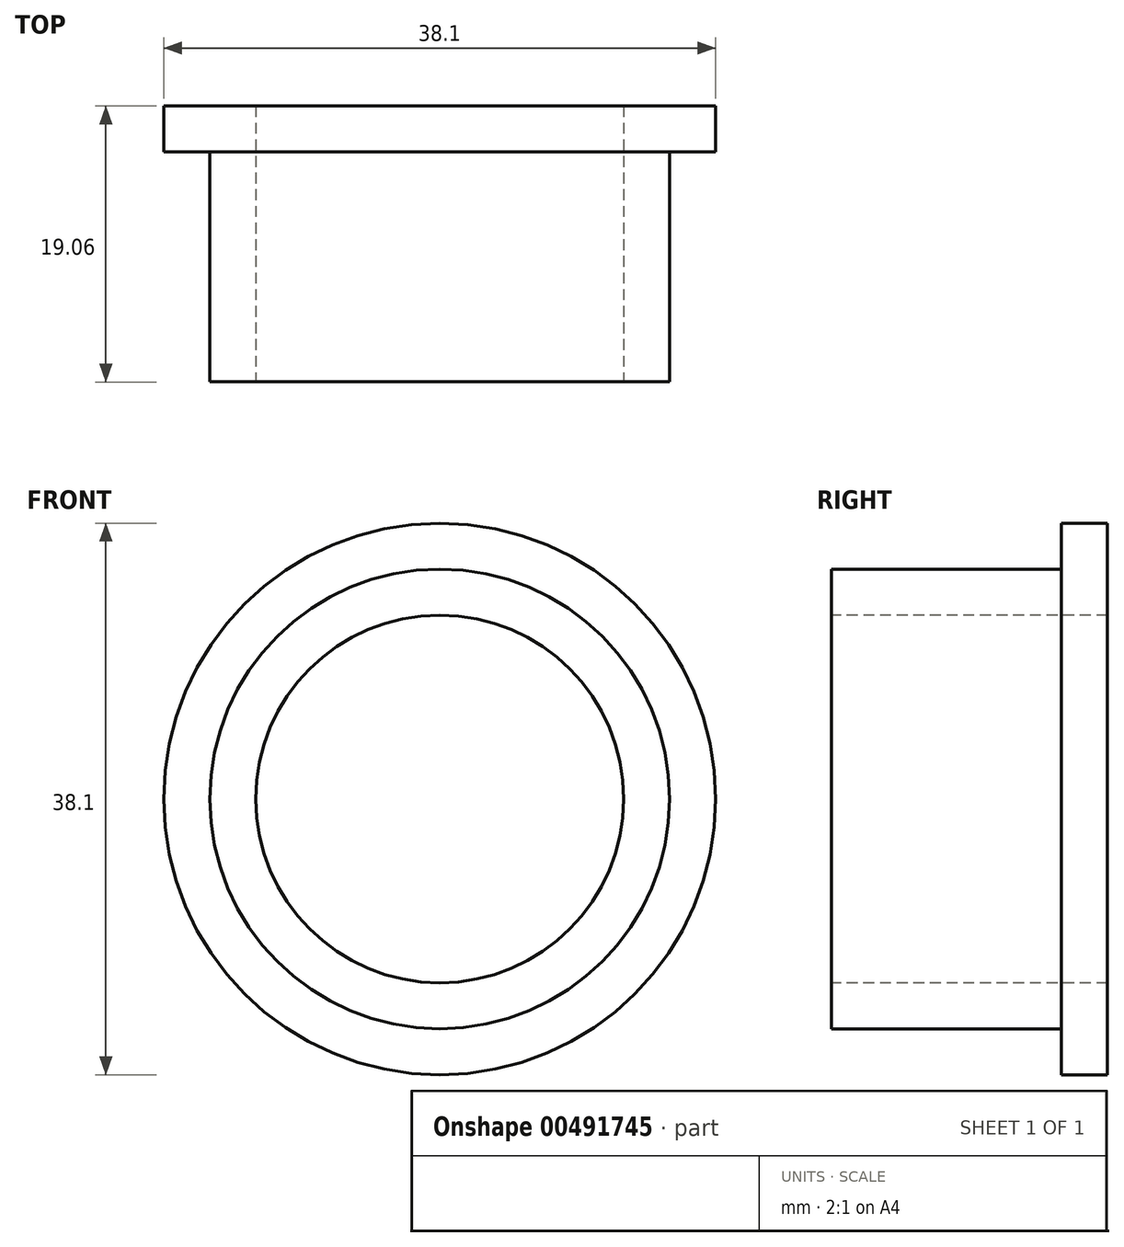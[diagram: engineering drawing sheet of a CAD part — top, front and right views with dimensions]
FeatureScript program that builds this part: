
annotation { "Feature Type Name" : "Feature", "Feature Type Description" : "" }
export const myFeature = defineFeature(function(context is Context, id is Id, definition is map)
    precondition{}
    {
        {
            var Q0;
            Q0=qCreatedBy(makeId("Right.planeOp"),FACE);
            var sketch = newSketch(context, id + "F0", { "sketchPlane" : qUnion([Q0])});
            skLineSegment(sketch, "E0", {"start": v(0, 15.88) * mm, "end": v(0, 19.05) * mm});
            skLineSegment(sketch, "E1", {"start": v(0, 19.05) * mm, "end": v(3.17, 19.05) * mm});
            skLineSegment(sketch, "E2", {"start": v(3.17, 19.05) * mm, "end": v(3.17, 12.7) * mm});
            skLineSegment(sketch, "E3", {"start": v(3.17, 12.7) * mm, "end": v(-15.88, 12.7) * mm});
            skLineSegment(sketch, "E4", {"start": v(-15.88, 12.7) * mm, "end": v(-15.88, 15.87) * mm});
            skLineSegment(sketch, "E5", {"start": v(-15.88, 15.87) * mm, "end": v(0, 15.88) * mm});
            skLineSegment(sketch, "E6", {"start": v(-15.88, 0) * mm, "end": v(3.18, 0) * mm, "construction": true});
            skSolve(sketch);
        }
        {
            var Q0;
            Q0 = qSketchRegion(id + "F0", true);
            var Q1;
            Q1=sQuery(id+"F0.wireOp",EDGE,"E6");
            revolve(context, id + "F1", {"entities" : qUnion([Q0]), "axis" : qUnion([Q1]), "revolveType" : RevolveType.FULL});
        }
    });
